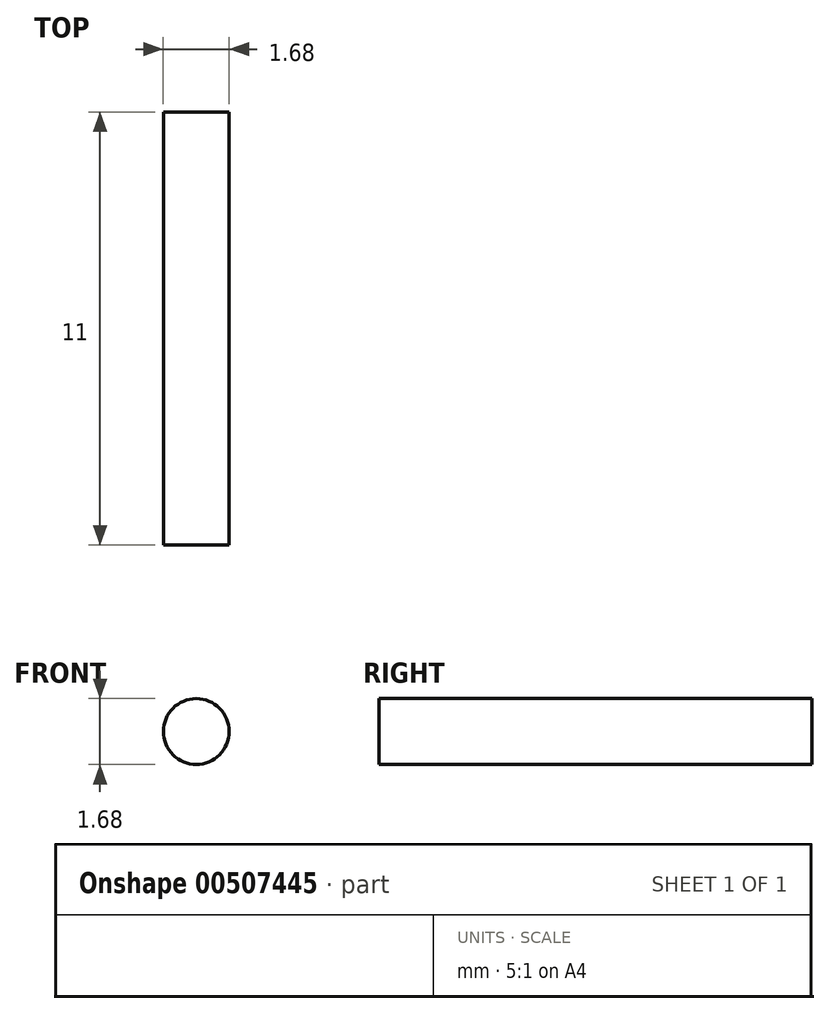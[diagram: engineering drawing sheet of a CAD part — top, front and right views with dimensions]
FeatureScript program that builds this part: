
annotation { "Feature Type Name" : "Feature", "Feature Type Description" : "" }
export const myFeature = defineFeature(function(context is Context, id is Id, definition is map)
    precondition{}
    {
        {
            var Q0;
            Q0=qCreatedBy(makeId("Front.planeOp"),FACE);
            var sketch = newSketch(context, id + "F0", { "sketchPlane" : qUnion([Q0])});
            skCircle(sketch, "E0", {"center": v(0, 0) * mm, "radius": 0.84 * mm});
            skSolve(sketch);
        }
        {
            var Q0;
            Q0 = qSketchRegion(id + "F0", true);
            extrude(context, id + "F1", {"entities" : qUnion([Q0]), "depth" : 11 * mm, "offsetDistance" : 25 * mm});
        }
    });
